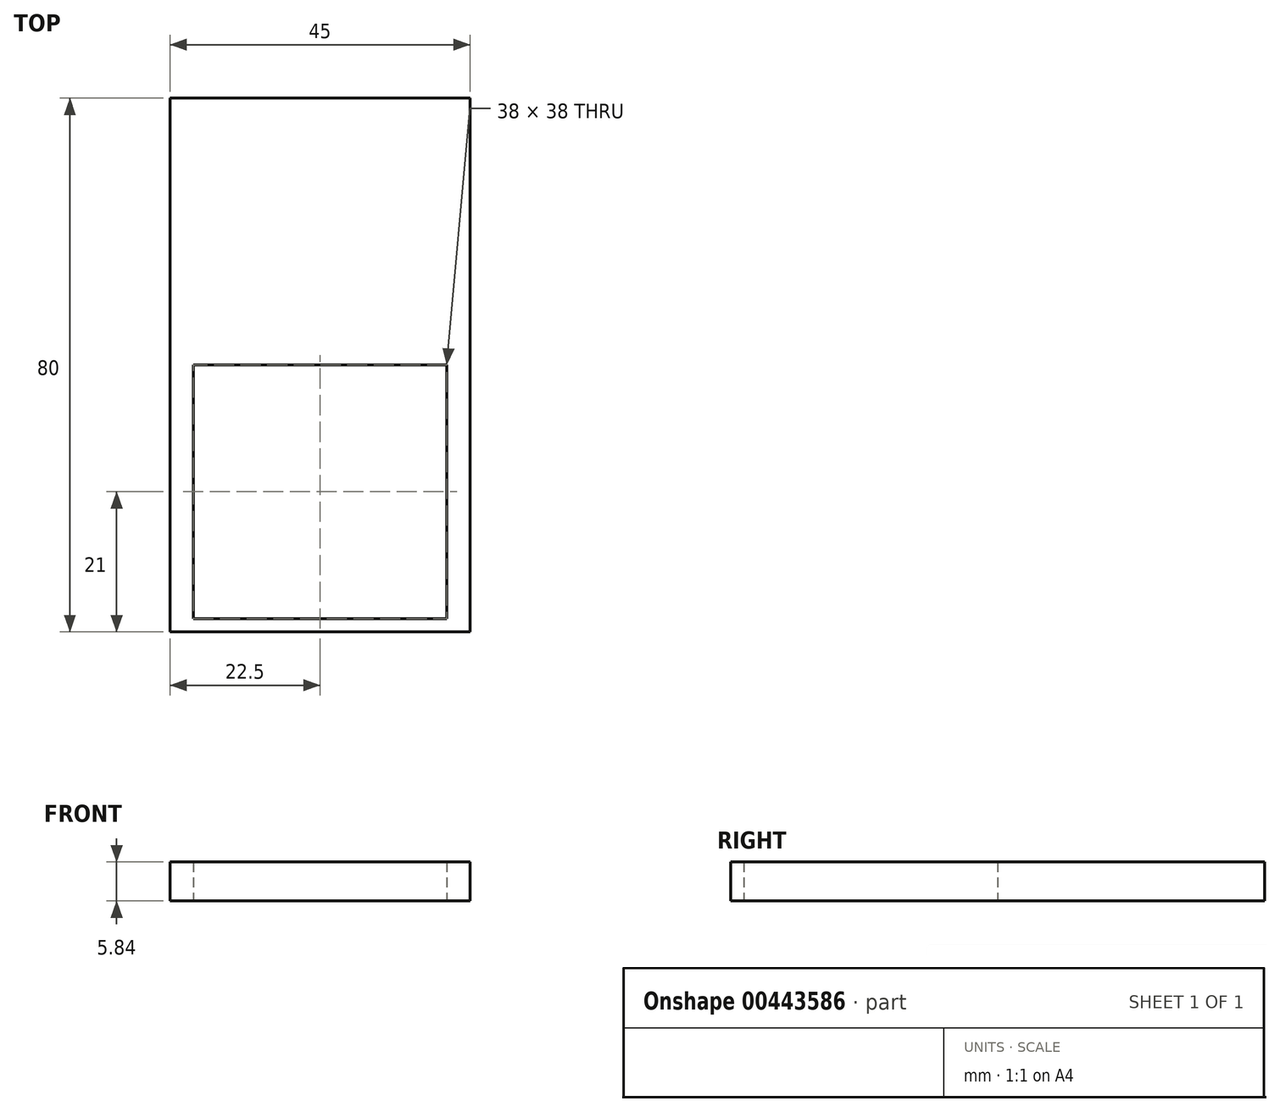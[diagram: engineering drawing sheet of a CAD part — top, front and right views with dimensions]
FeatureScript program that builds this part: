
annotation { "Feature Type Name" : "Feature", "Feature Type Description" : "" }
export const myFeature = defineFeature(function(context is Context, id is Id, definition is map)
    precondition{}
    {
        {
            var Q0;
            Q0=qCreatedBy(makeId("Top.planeOp"),FACE);
            var sketch = newSketch(context, id + "F0", { "sketchPlane" : qUnion([Q0])});
            skLineSegment(sketch, "E0.bottom", {"start": v(-22.5, 0) * mm, "end": v(22.5, 0) * mm});
            skLineSegment(sketch, "E0.top", {"start": v(-22.5, 80) * mm, "end": v(22.5, 80) * mm});
            skLineSegment(sketch, "E0.left", {"start": v(-22.5, 0) * mm, "end": v(-22.5, 80) * mm});
            skLineSegment(sketch, "E0.right", {"start": v(22.5, 0) * mm, "end": v(22.5, 80) * mm});
            skLineSegment(sketch, "E1.bottom", {"start": v(-19, 40) * mm, "end": v(19, 40) * mm});
            skLineSegment(sketch, "E1.top", {"start": v(-19, 2) * mm, "end": v(19, 2) * mm});
            skLineSegment(sketch, "E1.left", {"start": v(-19, 40) * mm, "end": v(-19, 2) * mm});
            skLineSegment(sketch, "E1.right", {"start": v(19, 40) * mm, "end": v(19, 2) * mm});
            skPoint(sketch, "E2", {"position": v(-22.5, 40) * mm});
            skPoint(sketch, "E3", {"position": v(22.5, 40) * mm});
            skPoint(sketch, "E4", {"position": v(0, 40) * mm});
            skSolve(sketch);
        }
        {
            var Q0;
            Q0=qSketchRegion(id+"F0",true);
            extrude(context, id + "F1", {"entities" : qUnion([Q0]), "depth" : 5.84 * mm});
        }
    });
